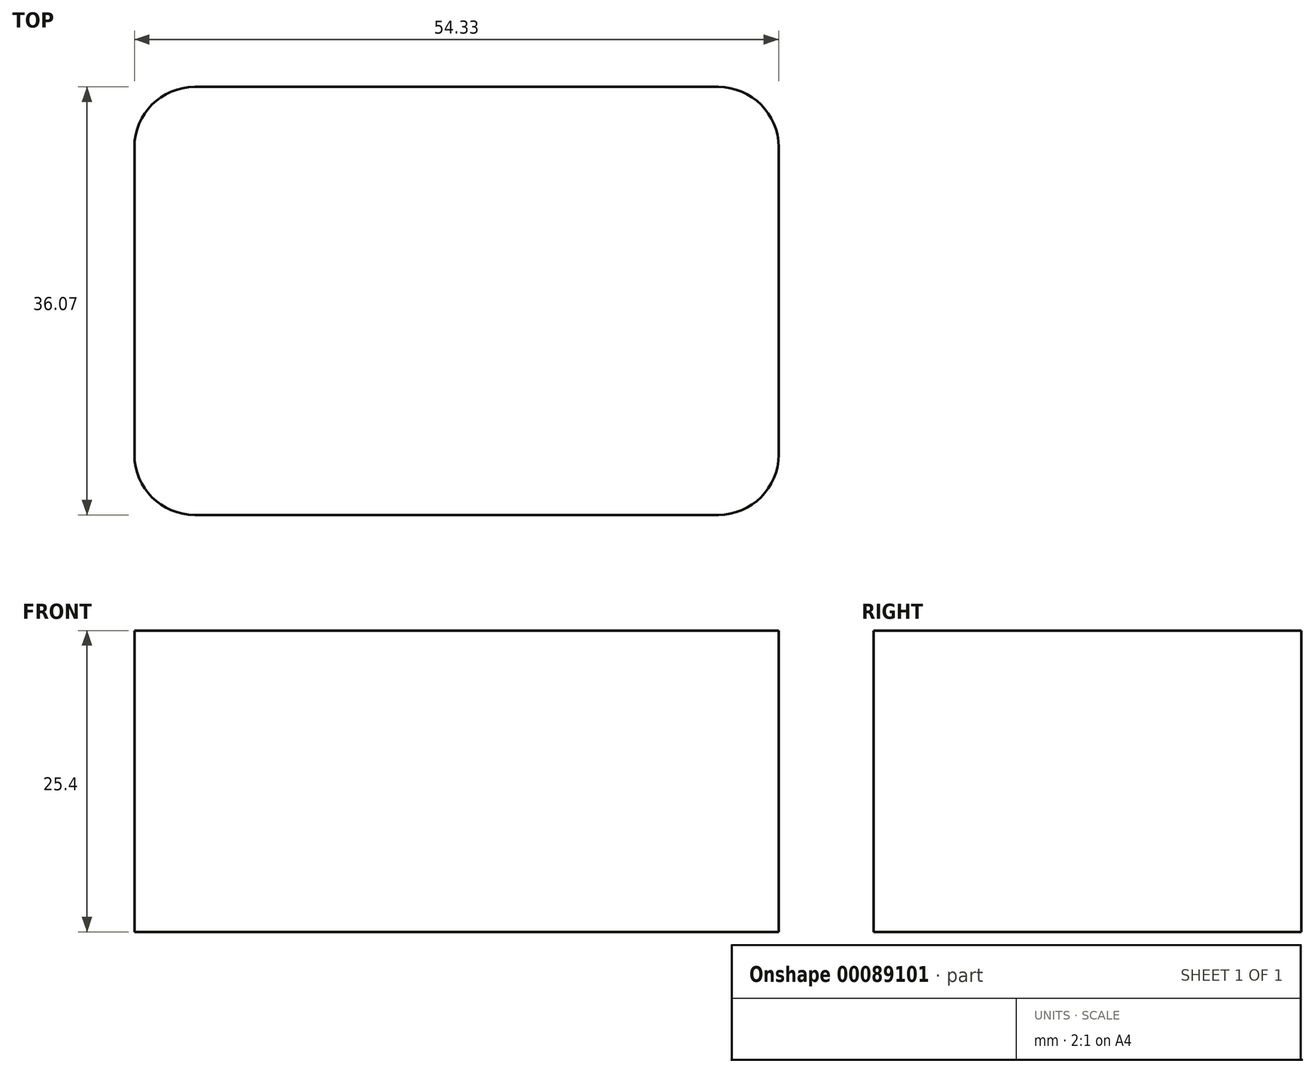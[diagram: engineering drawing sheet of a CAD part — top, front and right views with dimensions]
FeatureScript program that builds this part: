
annotation { "Feature Type Name" : "Feature", "Feature Type Description" : "" }
export const myFeature = defineFeature(function(context is Context, id is Id, definition is map)
    precondition{}
    {
        {
            var Q0;
            Q0=qCreatedBy(makeId("Top.planeOp"),FACE);
            var sketch = newSketch(context, id + "F0", { "sketchPlane" : qUnion([Q0])});
            skLineSegment(sketch, "E0.bottom", {"start": v(0, 0) * mm, "end": v(54.33, 0) * mm});
            skLineSegment(sketch, "E0.top", {"start": v(0, -36.07) * mm, "end": v(54.33, -36.07) * mm});
            skLineSegment(sketch, "E0.left", {"start": v(0, 0) * mm, "end": v(0, -36.07) * mm});
            skLineSegment(sketch, "E0.right", {"start": v(54.33, 0) * mm, "end": v(54.33, -36.07) * mm});
            skSolve(sketch);
        }
        {
            var Q0;
            Q0 = qSketchRegion(id + "F0", true);
            extrude(context, id + "F1", {"entities" : qUnion([Q0]), "depth" : 25.4 * mm});
        }
        {
            var Q0;
            Q0=makeQuery(id+"F1.opExtrude","SWEPT_EDGE",EDGE,{"disambiguationData":[OSD([sQuery(id+"F0.wireOp",EDGE,"E0.top"),sQuery(id+"F0.wireOp",EDGE,"E0.left")])]});
            var Q1;
            Q1=makeQuery(id+"F1.opExtrude","SWEPT_EDGE",EDGE,{"disambiguationData":[OSD([sQuery(id+"F0.wireOp",EDGE,"E0.bottom"),sQuery(id+"F0.wireOp",EDGE,"E0.left")])]});
            var Q2;
            Q2=makeQuery(id+"F1.opExtrude","SWEPT_EDGE",EDGE,{"disambiguationData":[OSD([sQuery(id+"F0.wireOp",EDGE,"E0.top"),sQuery(id+"F0.wireOp",EDGE,"E0.right")])]});
            var Q3;
            Q3=makeQuery(id+"F1.opExtrude","SWEPT_EDGE",EDGE,{"disambiguationData":[OSD([sQuery(id+"F0.wireOp",EDGE,"E0.bottom"),sQuery(id+"F0.wireOp",EDGE,"E0.right")])]});
            fillet(context, id + "F2", {"entities" : qUnion([Q0, Q1, Q2, Q3]), "radius" : 5.08 * mm, "tangentPropagation" : true, "allowEdgeOverflow" : false});
        }
    });
